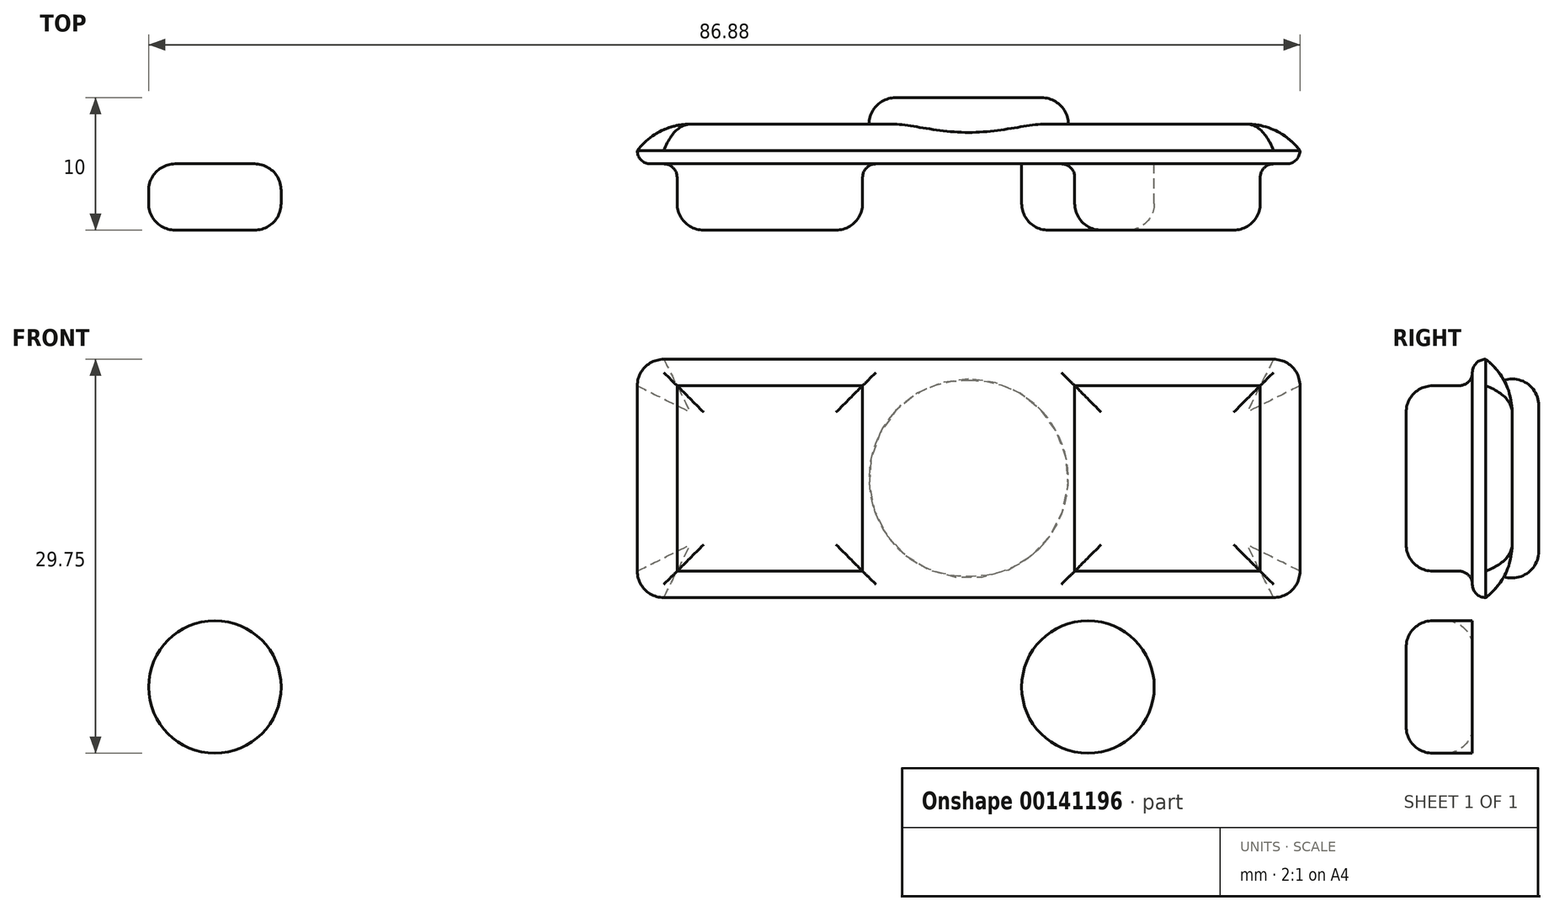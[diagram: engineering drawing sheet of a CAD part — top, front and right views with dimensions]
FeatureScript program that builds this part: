
annotation { "Feature Type Name" : "Feature", "Feature Type Description" : "" }
export const myFeature = defineFeature(function(context is Context, id is Id, definition is map)
    precondition{}
    {
        {
            var Q0;
            Q0=qCreatedBy(makeId("Front.planeOp"),FACE);
            var sketch = newSketch(context, id + "F0", { "sketchPlane" : qUnion([Q0])});
            skLineSegment(sketch, "E0.bottom", {"start": v(-18.7, 7.43) * mm, "end": v(31.3, 7.43) * mm});
            skLineSegment(sketch, "E0.top", {"start": v(-18.7, -10.57) * mm, "end": v(31.3, -10.57) * mm});
            skLineSegment(sketch, "E0.left", {"start": v(-18.7, 7.43) * mm, "end": v(-18.7, -10.57) * mm});
            skLineSegment(sketch, "E0.right", {"start": v(31.3, 7.43) * mm, "end": v(31.3, -10.57) * mm});
            skSolve(sketch);
        }
        {
            var Q0;
            Q0=makeQuery(id+"F0.imprint","IMPRINT",FACE,{"disambiguationData":[TD([[makeQuery(id+"F0.imprint","IMPRINT",EDGE,{"derivedFrom":sQuery(id+"F0.wireOp",EDGE,"E0.bottom")}),-1.0]])]});
            extrude(context, id + "F1", {"entities" : qUnion([Q0]), "depth" : 3 * mm, "offsetDistance" : 25 * mm});
        }
        {
            var Q0;
            Q0=makeQuery(id+"F1.opExtrude","CAP_FACE",FACE,{"disambiguationData":[OSD([sQuery(id+"F0.wireOp",EDGE,"E0.bottom"),sQuery(id+"F0.wireOp",EDGE,"E0.top"),sQuery(id+"F0.wireOp",EDGE,"E0.left"),sQuery(id+"F0.wireOp",EDGE,"E0.right")])],"isStart":false});
            var sketch = newSketch(context, id + "F2", { "sketchPlane" : qUnion([Q0])});
            skCircle(sketch, "E1", {"center": v(15.3, -17.32) * mm, "radius": 5 * mm});
            skCircle(sketch, "E2", {"center": v(15.8, -20.28) * mm, "radius": 5 * mm});
            skLineSegment(sketch, "E3.bottom", {"start": v(-15.7, 5.43) * mm, "end": v(-1.7, 5.43) * mm});
            skLineSegment(sketch, "E3.top", {"start": v(-15.7, -8.57) * mm, "end": v(-1.7, -8.57) * mm});
            skLineSegment(sketch, "E3.left", {"start": v(-15.7, 5.43) * mm, "end": v(-15.7, -8.57) * mm});
            skLineSegment(sketch, "E3.right", {"start": v(-1.7, 5.43) * mm, "end": v(-1.7, -8.57) * mm});
            skCircle(sketch, "E4", {"center": v(-50.57, -17.32) * mm, "radius": 5 * mm});
            skLineSegment(sketch, "E5.bottom", {"start": v(14.3, 5.43) * mm, "end": v(28.3, 5.43) * mm});
            skLineSegment(sketch, "E5.top", {"start": v(14.3, -8.57) * mm, "end": v(28.3, -8.57) * mm});
            skLineSegment(sketch, "E5.left", {"start": v(14.3, 5.43) * mm, "end": v(14.3, -8.57) * mm});
            skLineSegment(sketch, "E5.right", {"start": v(28.3, 5.43) * mm, "end": v(28.3, -8.57) * mm});
            skSolve(sketch);
        }
        {
            var Q0;
            Q0=makeQuery(id+"F2.imprint","IMPRINT",FACE,{"disambiguationData":[TD([[makeQuery(id+"F2.imprint","IMPRINT",EDGE,{"derivedFrom":sQuery(id+"F2.wireOp",EDGE,"ykoeOFHV-yia2-UwXg-Osyw-IsAJdHAODnss.bottom")}),-1.0]])]});
            var Q1;
            Q1=makeQuery(id+"F2.imprint","IMPRINT",FACE,{"disambiguationData":[TD([[makeQuery(id+"F2.imprint","IMPRINT",EDGE,{"derivedFrom":sQuery(id+"F2.wireOp",EDGE,"E1")}),1.0]])]});
            extrude(context, id + "F3", {"entities" : qUnion([Q0, Q1]), "operationType" : NewBodyOperationType.ADD, "depth" : 5 * mm, "offsetDistance" : 25 * mm});
        }
        {
            var Q0;
            Q0=makeQuery(id+"F1.opExtrude","CAP_FACE",FACE,{"disambiguationData":[OSD([sQuery(id+"F0.wireOp",EDGE,"E0.bottom"),sQuery(id+"F0.wireOp",EDGE,"E0.top"),sQuery(id+"F0.wireOp",EDGE,"E0.left"),sQuery(id+"F0.wireOp",EDGE,"E0.right")])],"isStart":true});
            var sketch = newSketch(context, id + "F4", { "sketchPlane" : qUnion([Q0])});
            skCircle(sketch, "E6", {"center": v(-6.3, -1.57) * mm, "radius": 7.52 * mm});
            skSolve(sketch);
        }
        {
            var Q0;
            Q0=makeQuery(id+"F4.imprint","IMPRINT",FACE,{"disambiguationData":[TD([[makeQuery(id+"F4.imprint","IMPRINT",EDGE,{"derivedFrom":sQuery(id+"F4.wireOp",EDGE,"E6")}),1.0]])]});
            extrude(context, id + "F5", {"entities" : qUnion([Q0]), "operationType" : NewBodyOperationType.ADD, "depth" : 2 * mm, "offsetDistance" : 25 * mm});
        }
        {
            var Q0;
            Q0=makeQuery(id+"F5.opExtrude","CAP_EDGE",EDGE,{"disambiguationData":[OSD([sQuery(id+"F4.wireOp",EDGE,"E6")])],"isStart":false});
            var Q1;
            Q1=makeQuery(id+"F3.opExtrude","CAP_EDGE",EDGE,{"disambiguationData":[OSD([sQuery(id+"F2.wireOp",EDGE,"E1")])],"isStart":false});
            var Q2;
            Q2=makeQuery(id+"F3.opExtrude","CAP_FACE",FACE,{"disambiguationData":[OSD([sQuery(id+"F2.wireOp",EDGE,"ykoeOFHV-yia2-UwXg-Osyw-IsAJdHAODnss.bottom"),sQuery(id+"F2.wireOp",EDGE,"ykoeOFHV-yia2-UwXg-Osyw-IsAJdHAODnss.top"),sQuery(id+"F2.wireOp",EDGE,"ykoeOFHV-yia2-UwXg-Osyw-IsAJdHAODnss.left"),sQuery(id+"F2.wireOp",EDGE,"ykoeOFHV-yia2-UwXg-Osyw-IsAJdHAODnss.right")])],"isStart":false});
            fillet(context, id + "F6", {"entities" : qUnion([Q0, Q1, Q2]), "radius" : 2 * mm, "tangentPropagation" : true, "allowEdgeOverflow" : false});
        }
        {
            var Q0;
            Q0=makeQuery(id+"F1.opExtrude","CAP_FACE",FACE,{"disambiguationData":[OSD([sQuery(id+"F0.wireOp",EDGE,"E0.bottom"),sQuery(id+"F0.wireOp",EDGE,"E0.top"),sQuery(id+"F0.wireOp",EDGE,"E0.left"),sQuery(id+"F0.wireOp",EDGE,"E0.right")])],"isStart":false});
            fillet(context, id + "F7", {"entities" : qUnion([Q0]), "radius" : 1 * mm, "tangentPropagation" : true, "allowEdgeOverflow" : false});
        }
        {
            var Q0;
            Q0=makeQuery(id+"F1.opExtrude","SWEPT_EDGE",EDGE,{"disambiguationData":[OSD([sQuery(id+"F0.wireOp",EDGE,"E0.bottom"),sQuery(id+"F0.wireOp",EDGE,"E0.right")])]});
            var Q1;
            Q1=makeQuery(id+"F1.opExtrude","SWEPT_EDGE",EDGE,{"disambiguationData":[OSD([sQuery(id+"F0.wireOp",EDGE,"E0.top"),sQuery(id+"F0.wireOp",EDGE,"E0.right")])]});
            var Q2;
            Q2=makeQuery(id+"F1.opExtrude","SWEPT_EDGE",EDGE,{"disambiguationData":[OSD([sQuery(id+"F0.wireOp",EDGE,"E0.top"),sQuery(id+"F0.wireOp",EDGE,"E0.left")])]});
            var Q3;
            Q3=makeQuery(id+"F1.opExtrude","SWEPT_EDGE",EDGE,{"disambiguationData":[OSD([sQuery(id+"F0.wireOp",EDGE,"E0.bottom"),sQuery(id+"F0.wireOp",EDGE,"E0.left")])]});
            fillet(context, id + "F8", {"entities" : qUnion([Q0, Q1, Q2, Q3]), "radius" : 2 * mm, "tangentPropagation" : true, "allowEdgeOverflow" : false});
        }
        {
            var Q0;
            {var subQ0=sQuery(id+"F0.wireOp",EDGE,"E0.right");var subQ1=sQuery(id+"F0.wireOp",EDGE,"E0.bottom");Q0=makeQuery(id+"F8.opFillet","BLEND_EDGE",EDGE,{"blendedFrom":[makeQuery(id+"F1.opExtrude","SWEPT_EDGE",EDGE,{"disambiguationData":[OSD([subQ1,subQ0])]}),makeQuery(id+"F1.opExtrude","CAP_FACE",FACE,{"disambiguationData":[OSD([subQ1,sQuery(id+"F0.wireOp",EDGE,"E0.top"),sQuery(id+"F0.wireOp",EDGE,"E0.left"),subQ0])],"isStart":true})],"blendedInto":[makeQuery(id+"F1.opExtrude","CAP_FACE",FACE,{"disambiguationData":[OSD([subQ1,sQuery(id+"F0.wireOp",EDGE,"E0.top"),sQuery(id+"F0.wireOp",EDGE,"E0.left"),subQ0])],"isStart":true})]});}
            var Q1;
            Q1=makeQuery(id+"F1.opExtrude","CAP_EDGE",EDGE,{"disambiguationData":[OSD([sQuery(id+"F0.wireOp",EDGE,"E0.left")])],"isStart":true});
            fillet(context, id + "F9", {"entities" : qUnion([Q0, Q1]), "radius" : 5 * mm, "tangentPropagation" : true, "allowEdgeOverflow" : false});
        }
        {
            var Q0;
            Q0=makeQuery(id+"F2.imprint","IMPRINT",FACE,{"disambiguationData":[TD([[makeQuery(id+"F2.imprint","IMPRINT",EDGE,{"derivedFrom":sQuery(id+"F2.wireOp",EDGE,"E4")}),1.0]])]});
            extrude(context, id + "F10", {"entities" : qUnion([Q0]), "operationType" : NewBodyOperationType.ADD, "depth" : 5 * mm, "offsetDistance" : 25 * mm});
        }
        {
            var Q0;
            Q0=makeQuery(id+"F10.opExtrude","SWEPT_FACE",FACE,{"disambiguationData":[OSD([sQuery(id+"F2.wireOp",EDGE,"E4")])]});
            fillet(context, id + "F11", {"entities" : qUnion([Q0]), "radius" : 2 * mm, "tangentPropagation" : true, "allowEdgeOverflow" : false});
        }
        {
            var Q0;
            Q0=makeQuery(id+"F2.imprint","IMPRINT",FACE,{"disambiguationData":[TD([[makeQuery(id+"F2.imprint","IMPRINT",EDGE,{"derivedFrom":sQuery(id+"F2.wireOp",EDGE,"E3.bottom")}),-1.0]])]});
            var Q1;
            Q1=makeQuery(id+"F2.imprint","IMPRINT",FACE,{"disambiguationData":[TD([[makeQuery(id+"F2.imprint","IMPRINT",EDGE,{"derivedFrom":sQuery(id+"F2.wireOp",EDGE,"E5.bottom")}),-1.0]])]});
            extrude(context, id + "F12", {"entities" : qUnion([Q0, Q1]), "operationType" : NewBodyOperationType.ADD, "depth" : 5 * mm, "offsetDistance" : 25 * mm});
        }
        {
            var Q0;
            Q0=makeQuery(id+"F12.opExtrude","CAP_FACE",FACE,{"disambiguationData":[OSD([sQuery(id+"F2.wireOp",EDGE,"E3.bottom"),sQuery(id+"F2.wireOp",EDGE,"E3.top"),sQuery(id+"F2.wireOp",EDGE,"E3.left"),sQuery(id+"F2.wireOp",EDGE,"E3.right")])],"isStart":false});
            var Q1;
            Q1=makeQuery(id+"F12.opExtrude","CAP_FACE",FACE,{"disambiguationData":[OSD([sQuery(id+"F2.wireOp",EDGE,"E5.bottom"),sQuery(id+"F2.wireOp",EDGE,"E5.top"),sQuery(id+"F2.wireOp",EDGE,"E5.left"),sQuery(id+"F2.wireOp",EDGE,"E5.right")])],"isStart":false});
            fillet(context, id + "F13", {"entities" : qUnion([Q0, Q1]), "radius" : 2 * mm, "tangentPropagation" : true, "allowEdgeOverflow" : false});
        }
    });
